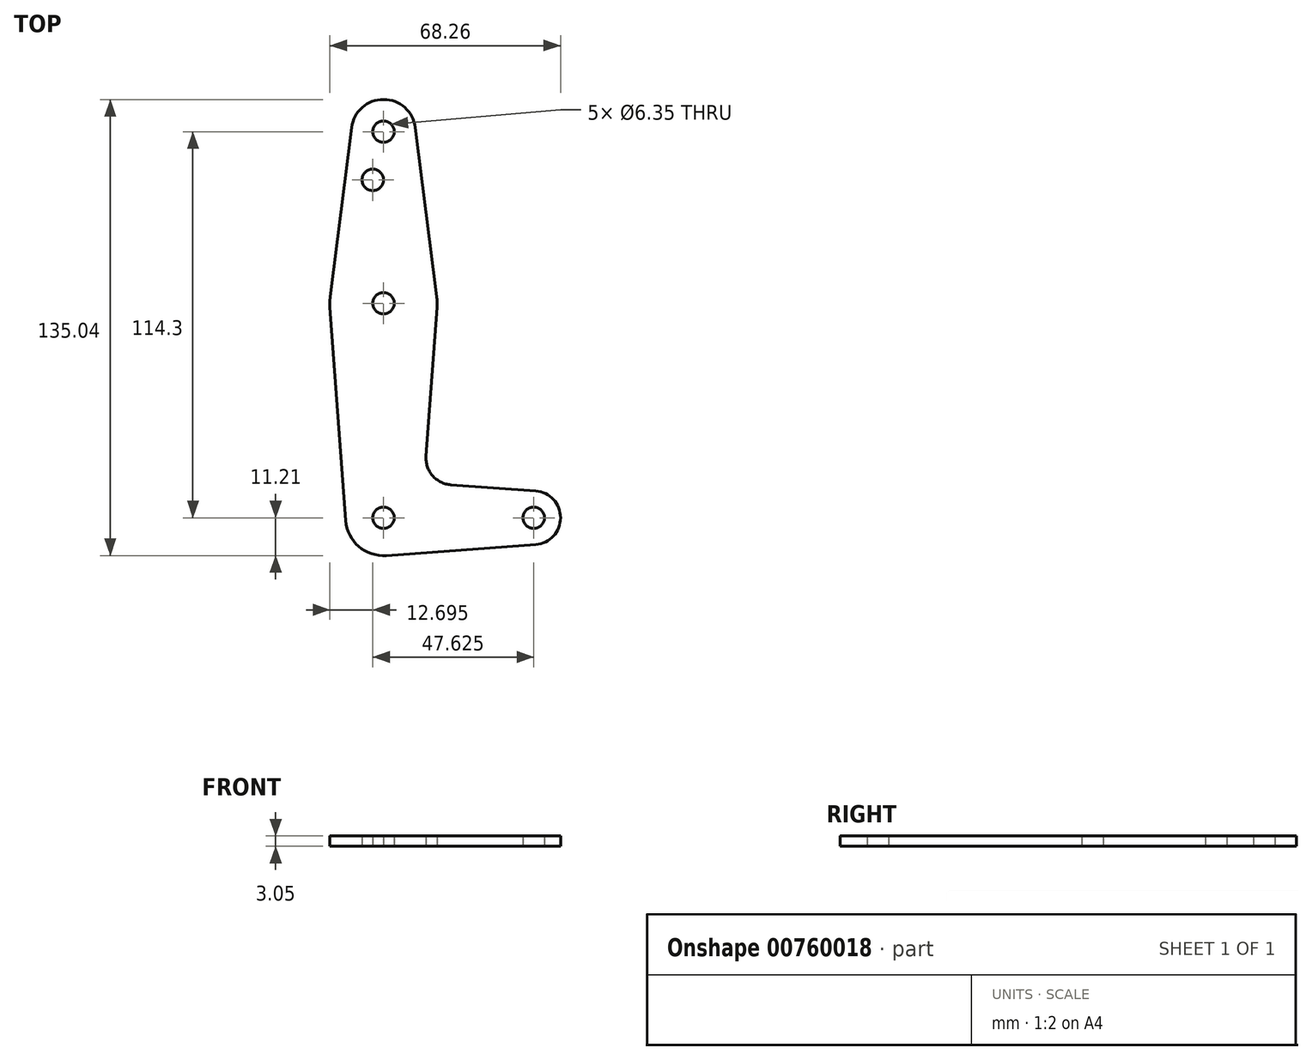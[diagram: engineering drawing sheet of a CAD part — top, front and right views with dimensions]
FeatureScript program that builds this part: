
annotation { "Feature Type Name" : "Feature", "Feature Type Description" : "" }
export const myFeature = defineFeature(function(context is Context, id is Id, definition is map)
    precondition{}
    {
        {
            var Q0;
            Q0=qCreatedBy(makeId("Top.planeOp"),FACE);
            var sketch = newSketch(context, id + "F0", { "sketchPlane" : qUnion([Q0])});
            skLineSegment(sketch, "E0", {"start": v(0, 114.3) * mm, "end": v(0, 0) * mm, "construction": true});
            skLineSegment(sketch, "E1", {"start": v(0, 0) * mm, "end": v(44.45, 0) * mm, "construction": true});
            skCircle(sketch, "E2", {"center": v(0, 114.3) * mm, "radius": 9.53 * mm});
            skCircle(sketch, "E3", {"center": v(0, 0) * mm, "radius": 11.2 * mm});
            skCircle(sketch, "E4", {"center": v(44.45, 0) * mm, "radius": 7.94 * mm});
            skCircle(sketch, "E5", {"center": v(0, 63.5) * mm, "radius": 15.88 * mm});
            skLineSegment(sketch, "E6", {"start": v(-9.45, 115.5) * mm, "end": v(-15.75, 65.48) * mm});
            skLineSegment(sketch, "E7", {"start": v(9.45, 115.5) * mm, "end": v(15.75, 65.48) * mm});
            skLineSegment(sketch, "E8", {"start": v(-15.83, 62.33) * mm, "end": v(-11.18, -0.82) * mm});
            skLineSegment(sketch, "E9", {"start": v(15.83, 62.33) * mm, "end": v(12.58, 18.28) * mm});
            skLineSegment(sketch, "E10", {"start": v(45.03, 7.92) * mm, "end": v(19.93, 9.77) * mm});
            skLineSegment(sketch, "E11", {"start": v(0.82, -11.18) * mm, "end": v(45.03, -7.92) * mm});
            skCircle(sketch, "E12", {"center": v(0, 114.3) * mm, "radius": 3.18 * mm});
            skCircle(sketch, "E13", {"center": v(0, 63.5) * mm, "radius": 3.18 * mm});
            skCircle(sketch, "E14", {"center": v(0, 0) * mm, "radius": 3.18 * mm});
            skCircle(sketch, "E15", {"center": v(44.45, 0) * mm, "radius": 3.18 * mm});
            skCircle(sketch, "E16", {"center": v(-3.18, 100.03) * mm, "radius": 3.18 * mm});
            skArc(sketch, "E17.filletArc", {"start": v(12.58, 18.28) * mm, "mid": v(14.5, 12.5) * mm, "end": v(19.93, 9.77) * mm});
            skSolve(sketch);
        }
        {
            var Q0;
            Q0 = qSketchRegion(id + "F0", true);
            extrude(context, id + "F1", {"entities" : qUnion([Q0]), "depth" : 3.05 * mm, "offsetDistance" : 25.4 * mm});
        }
    });
